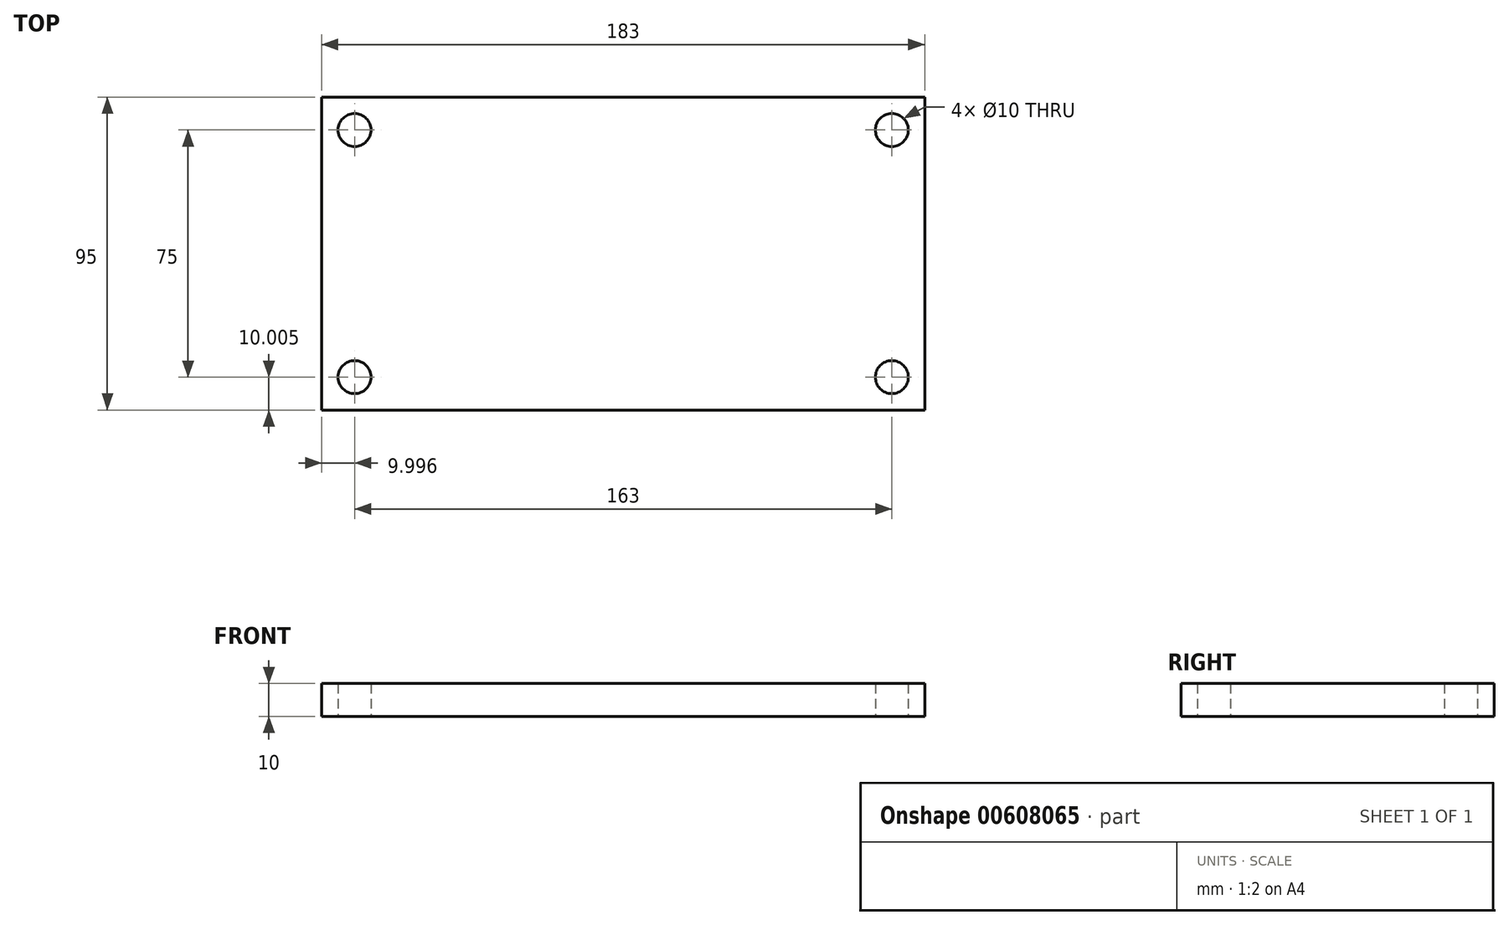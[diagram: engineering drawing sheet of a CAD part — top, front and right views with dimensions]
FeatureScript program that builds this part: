
annotation { "Feature Type Name" : "Feature", "Feature Type Description" : "" }
export const myFeature = defineFeature(function(context is Context, id is Id, definition is map)
    precondition{}
    {
        {
            var Q0;
            Q0=qCreatedBy(makeId("Top.planeOp"),FACE);
            var sketch = newSketch(context, id + "F0", { "sketchPlane" : qUnion([Q0])});
            skCircle(sketch, "E0", {"center": v(-39.34, 52.05) * mm, "radius": 5 * mm});
            skLineSegment(sketch, "E1", {"start": v(-39.34, 52.05) * mm, "end": v(123.66, 52.05) * mm, "construction": true});
            skCircle(sketch, "E2", {"center": v(123.66, 52.05) * mm, "radius": 5 * mm});
            skLineSegment(sketch, "E3", {"start": v(-39.34, 52.05) * mm, "end": v(-39.34, -22.95) * mm, "construction": true});
            skLineSegment(sketch, "E4", {"start": v(-39.34, -22.95) * mm, "end": v(123.66, -22.95) * mm, "construction": true});
            skLineSegment(sketch, "E5", {"start": v(123.66, -22.95) * mm, "end": v(123.66, 52.05) * mm, "construction": true});
            skCircle(sketch, "E6", {"center": v(-39.34, -22.95) * mm, "radius": 5 * mm});
            skCircle(sketch, "E7", {"center": v(123.66, -22.95) * mm, "radius": 5 * mm});
            skLineSegment(sketch, "E8.bottom", {"start": v(-49.34, 62.05) * mm, "end": v(133.66, 62.05) * mm});
            skLineSegment(sketch, "E8.top", {"start": v(-49.34, -32.95) * mm, "end": v(133.66, -32.95) * mm});
            skLineSegment(sketch, "E8.left", {"start": v(-49.34, 62.05) * mm, "end": v(-49.34, -32.95) * mm});
            skLineSegment(sketch, "E8.right", {"start": v(133.66, 62.05) * mm, "end": v(133.66, -32.95) * mm});
            skSolve(sketch);
        }
        {
            var Q0;
            Q0=makeQuery(id+"F0.imprint","IMPRINT",FACE,{"disambiguationData":[TD([[makeQuery(id+"F0.imprint","IMPRINT",EDGE,{"derivedFrom":sQuery(id+"F0.wireOp",EDGE,"E0")}),-1.0]])]});
            extrude(context, id + "F1", {"entities" : qUnion([Q0]), "depth" : 10 * mm, "offsetDistance" : 25 * mm});
        }
    });
